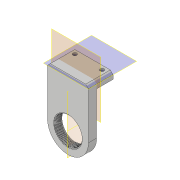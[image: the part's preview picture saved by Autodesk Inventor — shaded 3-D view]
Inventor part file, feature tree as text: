
AUTODESK INVENTOR PART (.ipt)
format: ipt  version: 2022 (Build 260153000, 153)  size: 378,368 bytes
history: native  units: mm
features: other x9, sketch x5, extrude x4, plane x3, reference x3, helix x1, fillet x1, chamfer x1, projected_geometry x1
ambient origin geometry x8: Origin, YZ Plane, XZ Plane, XY Plane, X Axis, Y Axis, Z Axis, Center Point
bodies: Solid1 (feature_tree)
feature tree (28):
  plane  "Work Plane1"
  extrude  "Extrusion1"  Depth=30.0mm
  extrude  "Extrusion2"  Depth=6.0mm TaperAngle=0.0deg
  plane  "Work Plane2"
  other  "Work Axis2"
  helix  "Coil1"  [1 undecoded]
  plane  "Arbeitsebene3"
  extrude  "Extrusion11"  Depth=9.95mm
  fillet  "Rundung1"  Radius=5.0mm
  chamfer  "Fase1"  Distance=15.0mm
  extrude  "Extrusion12"  Depth=10.0mm TaperAngle=45.0deg
  sketch  "Sketch1"  dims[d0=25.0mm d1=30.0mm]
  sketch  "Sketch2"  dims[d2=30.0mm d3=6.0mm d4=0.0mm d5=21.0mm]
  reference  "Reference3"
  reference  "Reference4"
  sketch  "Sketch6"  dims[d6=5.0mm d7=0.0mm]
  sketch  "Skizze11"  dims[d16=0.15mm d17=0.0mm d18=120.0deg d19=0.15mm d20=120.0deg d21=1.0mm d22=0.713333mm]
  reference  "Referenz9"
  sketch  "Skizze12"  dims[d25=0.713333mm d26=10.0mm d27=70.0mm d28=0.0mm d29=90.0deg d30=90.0deg d31=0.0mm d32=0.0mm d33=9.95mm d48=5.0mm d49=0.0mm d50=15.0mm d51=2.0mm d52=2.0mm d53=45.0deg d55=2.8mm d56=2.8mm d57=0.0mm d58=0.0mm d59=12.0mm d60=3.0mm d62=36.275mm d63=3.0mm d64=3.0mm d65=10.0mm d66=0.0mm]
  projected_geometry  "Projizierte Kontur5"
  other  "Assembly_Cube_Z_Focus_MGN_NEMA_v3.iam"
  other  "00_Microscope_Objective_Lens10x:1"
  other  "Assembly_Cube_empty_IM_v3:2"
  other  "10_Cube_1x1_IM:1"
  other  "Assembly_Cube_Z-Stage_NEMA11_china_v3.iam"
  other  "00_Linear_Stage_NEMA11_china:1"
  other  "Carriage:1"
  other  "30_Cube_Z_Focus_MGN_NEMA_slide:1"
note: 1 required parameter value undecoded (feature->parameter linkage not recoverable at this tier; creation-order binding heuristic only, values carry confidence <= 0.55)
